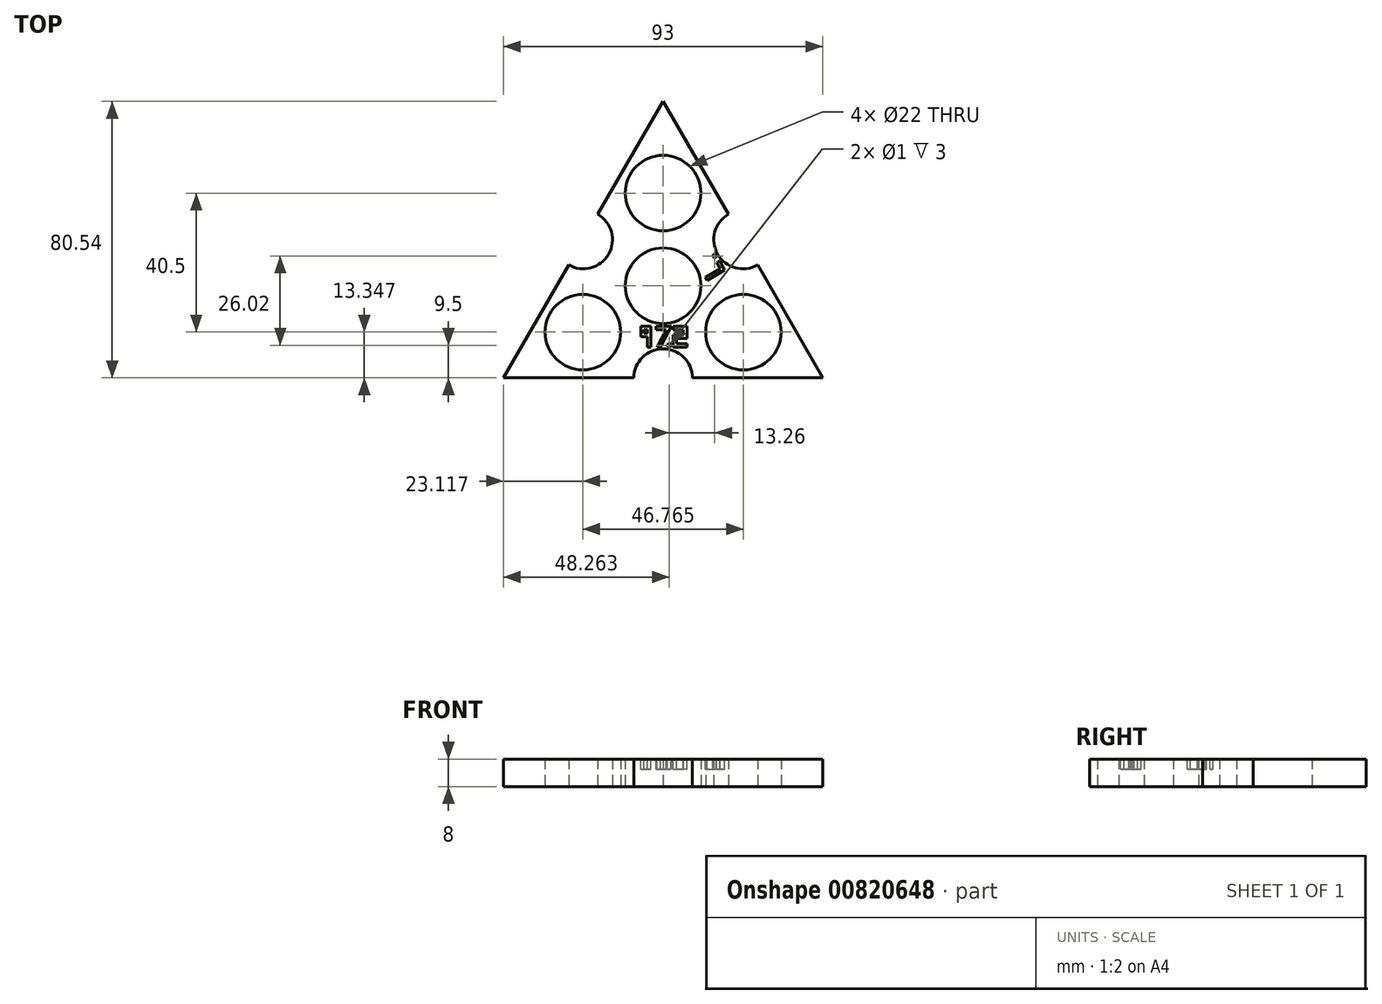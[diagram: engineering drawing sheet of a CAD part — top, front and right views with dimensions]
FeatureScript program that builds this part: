
annotation { "Feature Type Name" : "Feature", "Feature Type Description" : "" }
export const myFeature = defineFeature(function(context is Context, id is Id, definition is map)
    precondition{}
    {
        {
            var Q0;
            Q0=qCreatedBy(makeId("Top.planeOp"),FACE);
            var sketch = newSketch(context, id + "F0", { "sketchPlane" : qUnion([Q0])});
            skLineSegment(sketch, "E0", {"start": v(0, 0) * mm, "end": v(46.5, 0) * mm});
            skLineSegment(sketch, "E1", {"start": v(46.5, 0) * mm, "end": v(8.5, 0) * mm});
            skLineSegment(sketch, "E2", {"start": v(0, 80.54) * mm, "end": v(19, 47.63) * mm});
            skLineSegment(sketch, "E3", {"start": v(0, 80.54) * mm, "end": v(-19, 47.63) * mm});
            skCircle(sketch, "E4", {"center": v(0, 26.85) * mm, "radius": 11 * mm});
            skArc(sketch, "E5", {"start": v(-27.5, 32.9) * mm, "mid": v(-15.89, 36.02) * mm, "end": v(-19, 47.63) * mm});
            skArc(sketch, "E6", {"start": v(19, 47.63) * mm, "mid": v(15.89, 36.02) * mm, "end": v(27.5, 32.9) * mm});
            skArc(sketch, "E7", {"start": v(8.5, 0) * mm, "mid": v(0, 8.5) * mm, "end": v(-8.5, 0) * mm});
            skLineSegment(sketch, "E8.trimOffspring", {"start": v(-27.5, 32.9) * mm, "end": v(-46.5, 0) * mm});
            skLineSegment(sketch, "E9.trimOffspring", {"start": v(27.5, 32.9) * mm, "end": v(46.5, 0) * mm});
            skLineSegment(sketch, "E10.trimOffspring", {"start": v(-8.5, 0) * mm, "end": v(-46.5, 0) * mm});
            skCircle(sketch, "E11", {"center": v(-23.38, 13.35) * mm, "radius": 11 * mm});
            skPoint(sketch, "E12.orphan", {"position": v(-28.01, 10.67) * mm});
            skCircle(sketch, "E13", {"center": v(0, 53.85) * mm, "radius": 11 * mm});
            skCircle(sketch, "E14", {"center": v(23.38, 13.35) * mm, "radius": 11 * mm});
            skPoint(sketch, "E15.start.orphan", {"position": v(-9.53, 21.35) * mm});
            skSolve(sketch);
        }
        {
            var Q0;
            Q0=makeQuery(id+"F0.imprint","IMPRINT",FACE,{"disambiguationData":[TD([[makeQuery(id+"F0.imprint","IMPRINT",EDGE,{"derivedFrom":sQuery(id+"F0.wireOp",EDGE,"E2")}),-1.0]])]});
            extrude(context, id + "F1", {"entities" : qUnion([Q0]), "depth" : 8 * mm, "offsetDistance" : 25 * mm});
        }
        {
            var Q0;
            Q0=makeQuery(id+"F1.opExtrude","CAP_FACE",FACE,{"disambiguationData":[OSD([sQuery(id+"F0.wireOp",EDGE,"E0"),sQuery(id+"F0.wireOp",EDGE,"E2"),sQuery(id+"F0.wireOp",EDGE,"E3"),sQuery(id+"F0.wireOp",EDGE,"E4"),sQuery(id+"F0.wireOp",EDGE,"E5"),sQuery(id+"F0.wireOp",EDGE,"E6"),sQuery(id+"F0.wireOp",EDGE,"E7"),sQuery(id+"F0.wireOp",EDGE,"E8.trimOffspring"),sQuery(id+"F0.wireOp",EDGE,"E9.trimOffspring"),sQuery(id+"F0.wireOp",EDGE,"E10.trimOffspring"),sQuery(id+"F0.wireOp",EDGE,"E11"),sQuery(id+"F0.wireOp",EDGE,"E13"),sQuery(id+"F0.wireOp",EDGE,"E14")])],"isStart":false});
            var sketch = newSketch(context, id + "F2", { "sketchPlane" : qUnion([Q0])});
            skPoint(sketch, "E16.endSnap0", {"position": v(0, 8.5) * mm});
            skPoint(sketch, "E16.end.orphan", {"position": v(-4.57, 8.5) * mm});
            skLineSegment(sketch, "E17", {"start": v(13.96, 38.37) * mm, "end": v(13.46, 39.23) * mm});
            skPoint(sketch, "E18.start.orphan", {"position": v(15.89, 36.02) * mm});
            skLineSegment(sketch, "E19", {"start": v(-15.46, 35.77) * mm, "end": v(-10.46, 44.43) * mm});
            skLineSegment(sketch, "E20", {"start": v(-15.46, 35.77) * mm, "end": v(-20.46, 27.1) * mm});
            skPoint(sketch, "E21.start.orphan", {"position": v(-15.89, 36.02) * mm});
            skLineSegment(sketch, "E22", {"start": v(-15.46, 35.77) * mm, "end": v(-13.96, 38.37) * mm});
            skLineSegment(sketch, "E23", {"start": v(-13.96, 38.37) * mm, "end": v(-13.2, 39.67) * mm});
            skLineSegment(sketch, "E24", {"start": v(-2.1, 15) * mm, "end": v(2.45, 15) * mm});
            skPoint(sketch, "E25.start.orphan", {"position": v(-4.4, 9) * mm});
            skPoint(sketch, "E26.orphan", {"position": v(-3.46, 9) * mm});
            skPoint(sketch, "E27.end.orphan", {"position": v(-3.67, 12.4) * mm});
            skPoint(sketch, "E27.start.orphan", {"position": v(-3.46, 12) * mm});
            skLineSegment(sketch, "E28", {"start": v(-2.1, 15) * mm, "end": v(-2.1, 14) * mm});
            skLineSegment(sketch, "E29", {"start": v(-2.1, 14) * mm, "end": v(0.9, 14) * mm});
            skPoint(sketch, "E30.orphan", {"position": v(-3.46, 15) * mm});
            skPoint(sketch, "E31.trimOffspring.end.orphan", {"position": v(-10.97, 15) * mm});
            skPoint(sketch, "E31.trimOffspring.start.orphan", {"position": v(-5.67, 14.4) * mm});
            skLineSegment(sketch, "E32", {"start": v(0.9, 14) * mm, "end": v(-1.82, 9) * mm});
            skLineSegment(sketch, "E33", {"start": v(-1.82, 9) * mm, "end": v(-0.82, 9) * mm});
            skLineSegment(sketch, "E34", {"start": v(-0.82, 9) * mm, "end": v(2.45, 15) * mm});
            skLineSegment(sketch, "E35", {"start": v(6.91, 9) * mm, "end": v(2.91, 9) * mm});
            skLineSegment(sketch, "E36", {"start": v(2.91, 9) * mm, "end": v(2.91, 11.5) * mm});
            skLineSegment(sketch, "E37", {"start": v(6.91, 9) * mm, "end": v(6.91, 10) * mm});
            skLineSegment(sketch, "E38", {"start": v(6.91, 10) * mm, "end": v(3.91, 10) * mm});
            skLineSegment(sketch, "E39", {"start": v(3.91, 11.5) * mm, "end": v(6.91, 11.5) * mm});
            skLineSegment(sketch, "E40", {"start": v(3.91, 10) * mm, "end": v(3.91, 11.5) * mm});
            skLineSegment(sketch, "E41", {"start": v(2.91, 11.5) * mm, "end": v(2.91, 12.5) * mm});
            skLineSegment(sketch, "E42", {"start": v(2.91, 12.5) * mm, "end": v(5.91, 12.5) * mm});
            skLineSegment(sketch, "E43", {"start": v(6.91, 11.5) * mm, "end": v(6.91, 15) * mm});
            skLineSegment(sketch, "E44", {"start": v(6.91, 15) * mm, "end": v(2.86, 15) * mm});
            skLineSegment(sketch, "E45", {"start": v(2.86, 15) * mm, "end": v(2.86, 14) * mm});
            skLineSegment(sketch, "E46", {"start": v(2.86, 14) * mm, "end": v(5.86, 14) * mm});
            skLineSegment(sketch, "E47", {"start": v(5.86, 14) * mm, "end": v(5.91, 12.5) * mm});
            skLineSegment(sketch, "E48", {"start": v(-4.54, 12) * mm, "end": v(-4.54, 9) * mm});
            skLineSegment(sketch, "E49", {"start": v(-4.54, 9) * mm, "end": v(-3.54, 9) * mm});
            skLineSegment(sketch, "E50", {"start": v(-3.54, 9) * mm, "end": v(-3.54, 12) * mm});
            skLineSegment(sketch, "E51", {"start": v(-3.54, 12) * mm, "end": v(-3.54, 15) * mm});
            skPoint(sketch, "E52.center.orphan", {"position": v(-4.67, 13.4) * mm});
            skLineSegment(sketch, "E53", {"start": v(-3.54, 15) * mm, "end": v(-6.54, 15) * mm});
            skLineSegment(sketch, "E54", {"start": v(-6.54, 15) * mm, "end": v(-6.54, 12) * mm});
            skLineSegment(sketch, "E55", {"start": v(-6.54, 12) * mm, "end": v(-4.54, 12) * mm});
            skLineSegment(sketch, "E56", {"start": v(-4.54, 13) * mm, "end": v(-5.54, 13) * mm});
            skLineSegment(sketch, "E57", {"start": v(-5.54, 13) * mm, "end": v(-5.54, 14) * mm});
            skLineSegment(sketch, "E58", {"start": v(-5.54, 14) * mm, "end": v(-4.54, 14) * mm});
            skLineSegment(sketch, "E59", {"start": v(-4.54, 14) * mm, "end": v(-4.54, 13) * mm});
            skPoint(sketch, "E60.center.orphan", {"position": v(-5.04, 13.5) * mm});
            skLineSegment(sketch, "E61", {"start": v(17.96, 31.44) * mm, "end": v(12.76, 28.44) * mm});
            skLineSegment(sketch, "E62", {"start": v(12.76, 28.44) * mm, "end": v(12.26, 29.3) * mm});
            skLineSegment(sketch, "E63", {"start": v(12.26, 29.3) * mm, "end": v(16.59, 31.8) * mm});
            skLineSegment(sketch, "E64", {"start": v(16.59, 31.8) * mm, "end": v(15.59, 33.54) * mm});
            skLineSegment(sketch, "E65", {"start": v(15.59, 33.54) * mm, "end": v(16.46, 34.04) * mm});
            skCircle(sketch, "E66", {"center": v(1.76, 9.5) * mm, "radius": 0.5 * mm});
            skPoint(sketch, "E67.orphan", {"position": v(1.26, 10) * mm});
            skLineSegment(sketch, "E68.trimOffspring", {"start": v(2.91, 9) * mm, "end": v(6.91, 9) * mm});
            skLineSegment(sketch, "E69.trimOffspring", {"start": v(2.86, 15) * mm, "end": v(6.91, 15) * mm});
            skPoint(sketch, "E70.bottom.start.orphan", {"position": v(2.26, 9) * mm});
            skPoint(sketch, "E71.orphan", {"position": v(-0.1, 9) * mm});
            skLineSegment(sketch, "E72.trimOffspring", {"start": v(-0.82, 9) * mm, "end": v(-1.82, 9) * mm});
            skPoint(sketch, "E73.end.orphan", {"position": v(0.9, 9) * mm});
            skPoint(sketch, "E73.start.orphan", {"position": v(0.6, 9) * mm});
            skLineSegment(sketch, "E74.trimOffspring", {"start": v(-3.46, 9) * mm, "end": v(-4.54, 9) * mm});
            skPoint(sketch, "E75.orphan", {"position": v(-9.4, 9) * mm});
            skCircle(sketch, "E76", {"center": v(15.02, 35.52) * mm, "radius": 0.5 * mm});
            skPoint(sketch, "E77.orphan", {"position": v(14.84, 34.84) * mm});
            skLineSegment(sketch, "E78", {"start": v(13.46, 39.23) * mm, "end": v(13.96, 38.37) * mm});
            skLineSegment(sketch, "E79", {"start": v(13.96, 38.37) * mm, "end": v(8.76, 35.37) * mm});
            skLineSegment(sketch, "E80", {"start": v(13.46, 39.23) * mm, "end": v(11.3, 37.98) * mm});
            skLineSegment(sketch, "E81", {"start": v(8.76, 35.37) * mm, "end": v(8.26, 36.23) * mm});
            skLineSegment(sketch, "E82", {"start": v(8.26, 36.23) * mm, "end": v(10.42, 37.48) * mm});
            skLineSegment(sketch, "E83", {"start": v(11.3, 37.98) * mm, "end": v(10.3, 39.72) * mm});
            skLineSegment(sketch, "E84", {"start": v(10.3, 39.72) * mm, "end": v(12.46, 40.97) * mm});
            skLineSegment(sketch, "E85", {"start": v(12.46, 40.97) * mm, "end": v(11.96, 41.83) * mm});
            skLineSegment(sketch, "E86", {"start": v(10.42, 37.48) * mm, "end": v(9.42, 39.22) * mm});
            skLineSegment(sketch, "E87", {"start": v(11.96, 41.83) * mm, "end": v(6.76, 38.83) * mm});
            skLineSegment(sketch, "E88", {"start": v(6.76, 38.83) * mm, "end": v(7.26, 37.97) * mm});
            skLineSegment(sketch, "E89", {"start": v(7.26, 37.97) * mm, "end": v(9.42, 39.22) * mm});
            skPoint(sketch, "E90.orphan", {"position": v(20.46, 27.1) * mm});
            skLineSegment(sketch, "E91.trimOffspring", {"start": v(16.46, 34.04) * mm, "end": v(17.96, 31.44) * mm});
            skPoint(sketch, "E92.orphan", {"position": v(15.7, 35.34) * mm});
            skPoint(sketch, "E93.orphan", {"position": v(10.46, 44.43) * mm});
            skPoint(sketch, "E94.start.orphan", {"position": v(12.96, 40.1) * mm});
            skPoint(sketch, "E95.end.orphan", {"position": v(15.2, 36.2) * mm});
            skPoint(sketch, "E95.start.orphan", {"position": v(15.46, 35.77) * mm});
            skSolve(sketch);
        }
        {
            var Q0;
            {var subQ0=sQuery(id+"F2.wireOp",EDGE,"E48");Q0=makeQuery(id+"F2.imprint","IMPRINT",FACE,{"disambiguationData":[TD([[makeQuery(id+"F2.imprint","IMPRINT",EDGE,{"derivedFrom":subQ0}),1.0]])]});}
            var Q1;
            Q1=makeQuery(id+"F2.imprint","IMPRINT",FACE,{"disambiguationData":[TD([[makeQuery(id+"F2.imprint","IMPRINT",EDGE,{"derivedFrom":sQuery(id+"F2.wireOp",EDGE,"E24")}),-1.0]])]});
            var Q2;
            Q2=makeQuery(id+"F2.imprint","IMPRINT",FACE,{"disambiguationData":[TD([[makeQuery(id+"F2.imprint","IMPRINT",EDGE,{"derivedFrom":sQuery(id+"F2.wireOp",EDGE,"E36")}),-1.0]])]});
            var Q3;
            Q3=makeQuery(id+"F2.imprint","IMPRINT",FACE,{"disambiguationData":[TD([[makeQuery(id+"F2.imprint","IMPRINT",EDGE,{"derivedFrom":sQuery(id+"F2.wireOp",EDGE,"E78")}),-1.0]])]});
            var Q4;
            Q4=makeQuery(id+"F2.imprint","IMPRINT",FACE,{"disambiguationData":[TD([[makeQuery(id+"F2.imprint","IMPRINT",EDGE,{"derivedFrom":sQuery(id+"F2.wireOp",EDGE,"E66")}),1.0]])]});
            var Q5;
            Q5=makeQuery(id+"F2.imprint","IMPRINT",FACE,{"disambiguationData":[TD([[makeQuery(id+"F2.imprint","IMPRINT",EDGE,{"derivedFrom":sQuery(id+"F2.wireOp",EDGE,"E76")}),1.0]])]});
            var Q6;
            Q6=makeQuery(id+"F2.imprint","IMPRINT",FACE,{"disambiguationData":[TD([[makeQuery(id+"F2.imprint","IMPRINT",EDGE,{"derivedFrom":sQuery(id+"F2.wireOp",EDGE,"E61")}),-1.0]])]});
            extrude(context, id + "F3", {"entities" : qUnion([Q0, Q1, Q2, Q3, Q4, Q5, Q6]), "operationType" : NewBodyOperationType.REMOVE, "oppositeDirection" : true, "depth" : 3 * mm, "offsetDistance" : 25 * mm});
        }
    });
